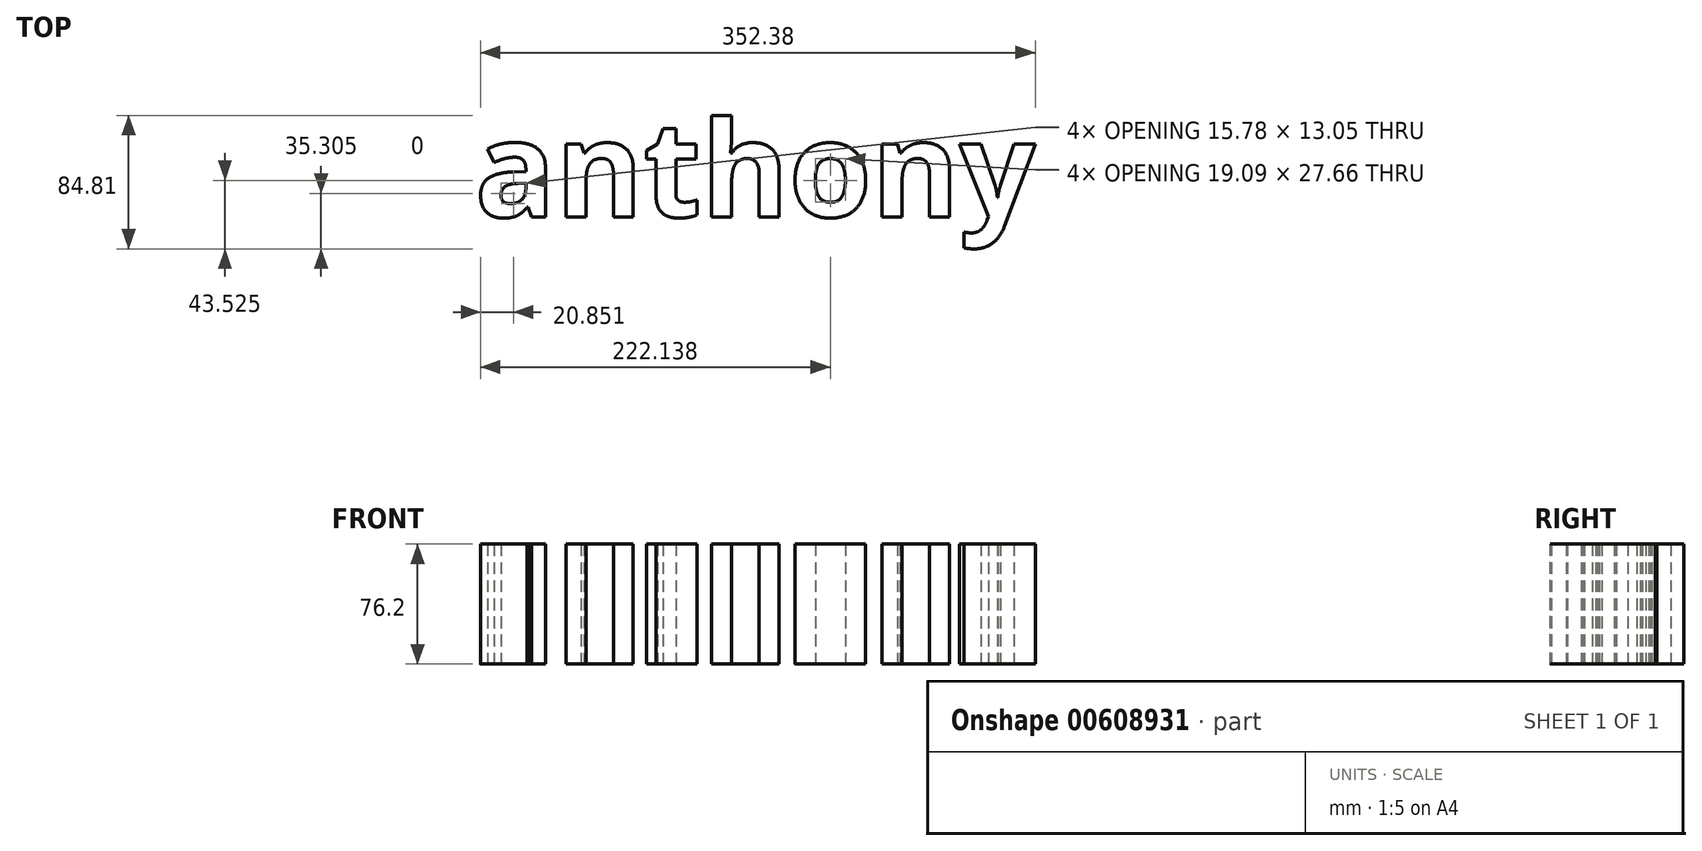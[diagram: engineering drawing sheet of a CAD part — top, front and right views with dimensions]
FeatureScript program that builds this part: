
annotation { "Feature Type Name" : "Feature", "Feature Type Description" : "" }
export const myFeature = defineFeature(function(context is Context, id is Id, definition is map)
    precondition{}
    {
        {
            var Q0;
            Q0=qCreatedBy(makeId("Top.planeOp"),FACE);
            var sketch = newSketch(context, id + "F0", { "sketchPlane" : qUnion([Q0])});
            skText(sketch, "E0", { "text": "anthony", "fontName": "OpenSans-Bold.ttf"});
            const initialGuessF0  = {"E0": [-0.15746, -0.02896, 1, 0, 0.06105]};
            skSetInitialGuess(sketch, initialGuessF0);
            skSolve(sketch);
        }
        {
            var Q0;
            Q0 = qSketchRegion(id + "F0", true);
            extrude(context, id + "F1", {"entities" : qUnion([Q0]), "depth" : 76.2 * mm, "offsetDistance" : 25.4 * mm});
        }
    });
